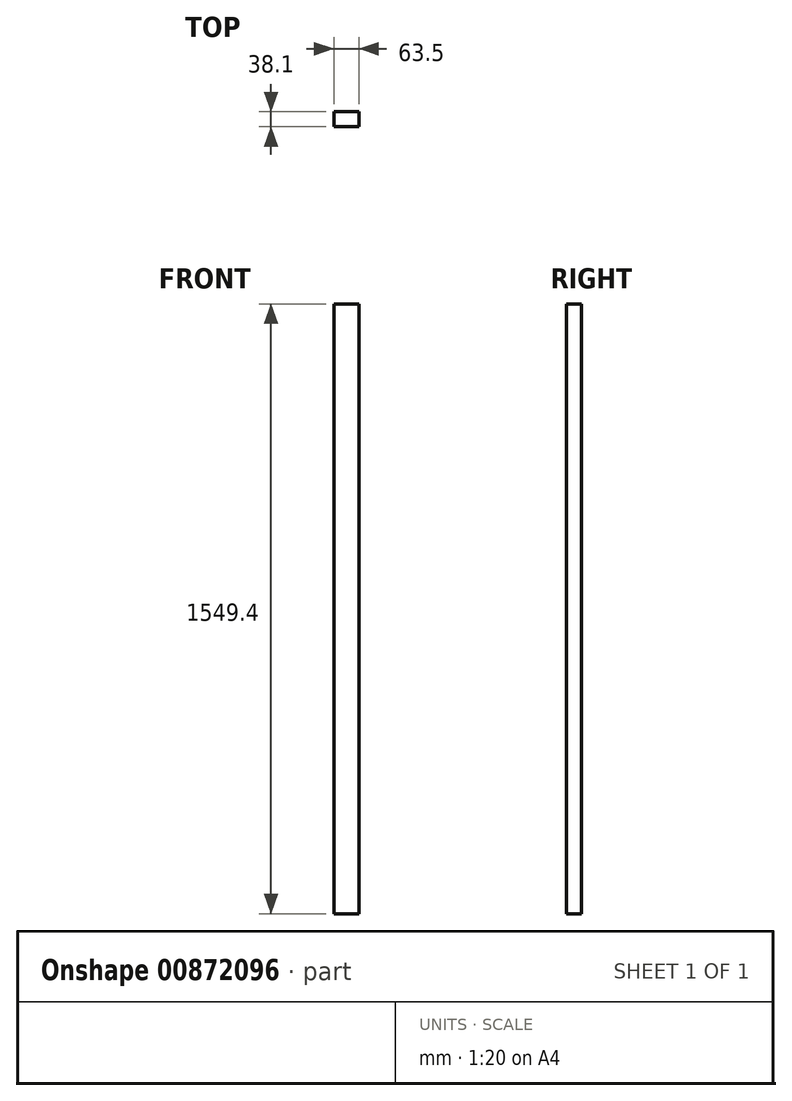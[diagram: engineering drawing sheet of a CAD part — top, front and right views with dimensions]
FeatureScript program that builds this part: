
annotation { "Feature Type Name" : "Feature", "Feature Type Description" : "" }
export const myFeature = defineFeature(function(context is Context, id is Id, definition is map)
    precondition{}
    {
        {
            var Q0;
            Q0=qCreatedBy(makeId("Front.planeOp"),FACE);
            var sketch = newSketch(context, id + "F0", { "sketchPlane" : qUnion([Q0])});
            skLineSegment(sketch, "E0.bottom", {"start": v(-3149.09, -1199.56) * mm, "end": v(-3212.59, -1199.56) * mm});
            skLineSegment(sketch, "E0.top", {"start": v(-3149.09, 349.84) * mm, "end": v(-3212.59, 349.84) * mm});
            skLineSegment(sketch, "E0.left", {"start": v(-3149.09, -1199.56) * mm, "end": v(-3149.09, 349.84) * mm});
            skLineSegment(sketch, "E0.right", {"start": v(-3212.59, -1199.56) * mm, "end": v(-3212.59, 349.84) * mm});
            skPoint(sketch, "E0.middle", {"position": v(-3180.84, -424.86) * mm});
            skSolve(sketch);
        }
        {
            var Q0;
            Q0 = qSketchRegion(id + "F0", true);
            extrude(context, id + "F1", {"entities" : qUnion([Q0]), "depth" : 38.1 * mm, "offsetDistance" : 25.4 * mm});
        }
    });
